# Revit family: Keilhauer-Symm-Seater_Bench_LAF_Arm-1
name_source: partatom
category: Furniture
units: mm (PartAtom-declared; Revit-internal decimal feet)

## family parameters
Always vertical = Yes
Cut with Voids When Loaded = No
OmniClass Number = 23.40.20.00
OmniClass Title = General Furniture and Specialties
Room Calculation Point = No
Shared = No
Work Plane-Based = No

## types (6) — shared parameters
Assembly Code = E2020200
Default Elevation = 0"
Depth = 31"
Height = 31"
Keynote = 12500
Low Emitting Finish = Yes
Low Emitting Material = Yes
Manufacturer = Keilhauer
Product Documentation Link = https://keilhauer.com
Revit Model Built By = https://servex-us.com
Salvage or Reuse = Yes
Type Comments = Symm
URL = https://keilhauer.com
Width Seat And Back Cushion = 27 3/4"
zero-valued in all types: Percentage of Recycled Content

## per-type parameters (varying)
| type | Description | Qty Seat And Back | Width |
| 93130 | 2-seater bench with LAF arm, 4-leg aluminum base | 2 | 58 3/4" |
| 93131 | 2-seater bench with LAF arm, 4-leg ash base | 2 | 58 3/4" |
| 93132 | 2-seater bench with LAF arm, 4-leg walnut base | 2 | 58 3/4" |
| 93230 | 3-seater bench with LAF arm, 4-leg aluminum base | 3 | 86 1/2" |
| 93231 | 3-seater bench with LAF arm, 4-leg ash base | 3 | 86 1/2" |
| 93232 | 3-seater bench with LAF arm, 4-leg walnut base | 3 | 86 1/2" |

note: column(s) folded — value = type name in every type: Model

## geometry (parser evidence)
native form markers: Sweep x7
no freeform markers — native parametric forms only
